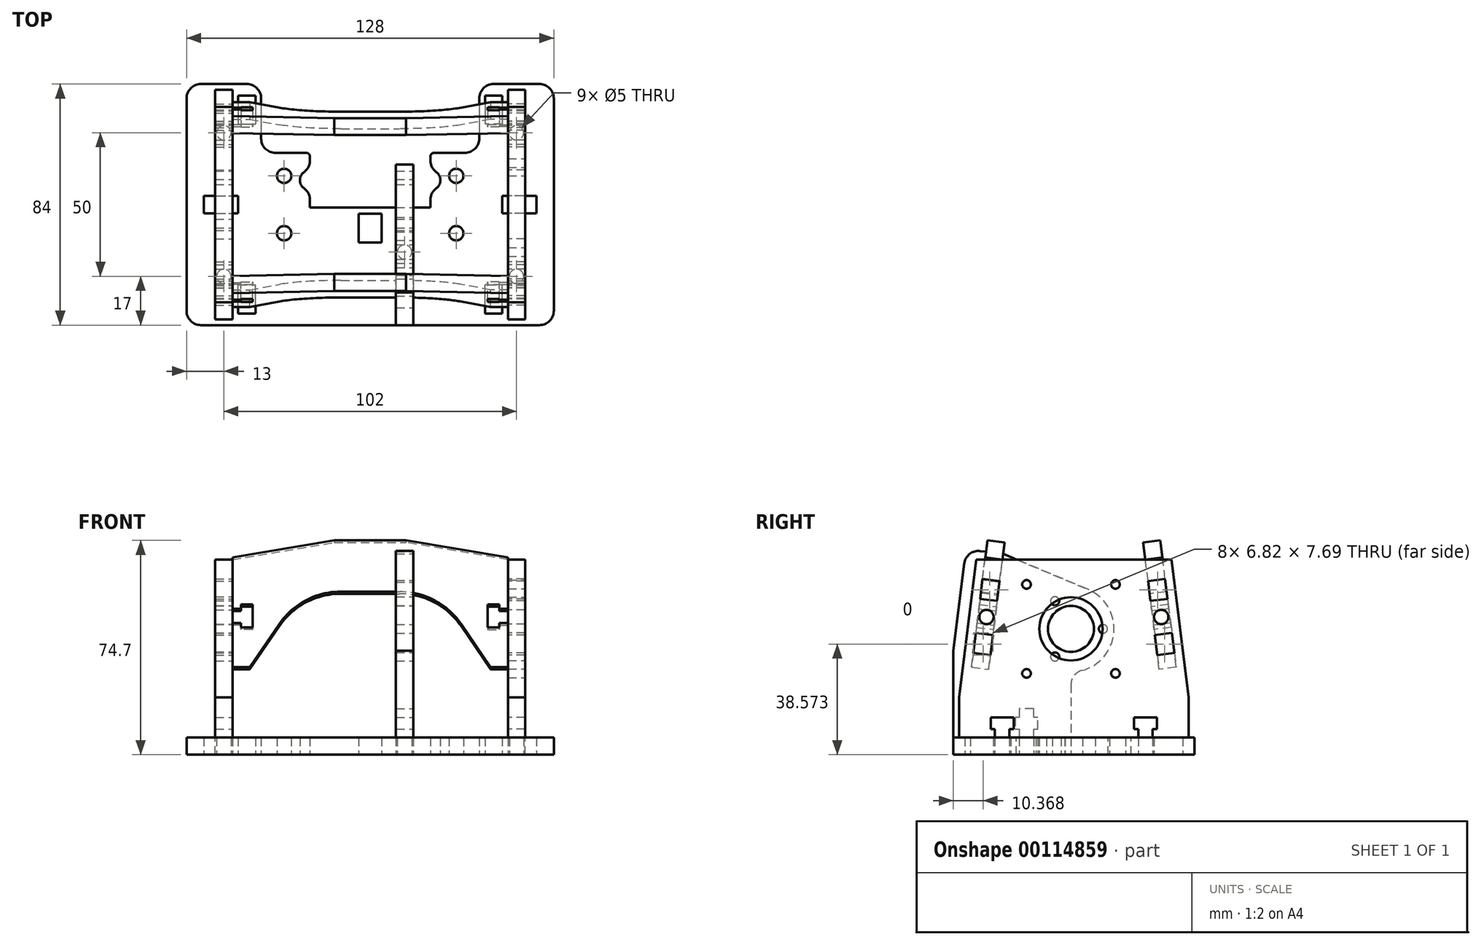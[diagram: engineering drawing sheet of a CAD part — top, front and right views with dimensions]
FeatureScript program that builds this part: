
annotation { "Feature Type Name" : "Feature", "Feature Type Description" : "" }
export const myFeature = defineFeature(function(context is Context, id is Id, definition is map)
    precondition{}
    {
        {
            var Q0;
            Q0=qCreatedBy(makeId("Top.planeOp"),FACE);
            var sketch = newSketch(context, id + "F0", { "sketchPlane" : qUnion([Q0])});
            skLineSegment(sketch, "E0.bottom", {"start": v(-59, 42) * mm, "end": v(-43, 42) * mm});
            skLineSegment(sketch, "E0.top", {"start": v(-59, -42) * mm, "end": v(59, -42) * mm});
            skLineSegment(sketch, "E0.left", {"start": v(-64, 37) * mm, "end": v(-64, -37) * mm});
            skLineSegment(sketch, "E0.right", {"start": v(64, 37) * mm, "end": v(64, -37) * mm});
            skPoint(sketch, "E1", {"position": v(0, 42) * mm});
            skPoint(sketch, "E2", {"position": v(-64, 0) * mm});
            skLineSegment(sketch, "E3.bottom", {"start": v(-46, 38) * mm, "end": v(-40, 38) * mm});
            skLineSegment(sketch, "E3.top", {"start": v(-46, 28) * mm, "end": v(-40, 28) * mm});
            skLineSegment(sketch, "E3.left", {"start": v(-46, 38) * mm, "end": v(-46, 28) * mm});
            skLineSegment(sketch, "E3.right", {"start": v(-40, 38) * mm, "end": v(-40, 28) * mm});
            skLineSegment(sketch, "E4.bottom", {"start": v(-58, 3) * mm, "end": v(-46, 3) * mm});
            skLineSegment(sketch, "E4.top", {"start": v(-58, -3) * mm, "end": v(-46, -3) * mm});
            skLineSegment(sketch, "E4.left", {"start": v(-58, 3) * mm, "end": v(-58, -3) * mm});
            skLineSegment(sketch, "E4.right", {"start": v(-46, 3) * mm, "end": v(-46, -3) * mm});
            skPoint(sketch, "E5", {"position": v(-58, 0) * mm});
            skLineSegment(sketch, "E6.MirrorCS", {"start": v(-40, -38) * mm, "end": v(-40, -28) * mm});
            skLineSegment(sketch, "E7.MirrorCS", {"start": v(-46, -38) * mm, "end": v(-40, -38) * mm});
            skLineSegment(sketch, "E8.MirrorCS", {"start": v(-46, -28) * mm, "end": v(-40, -28) * mm});
            skLineSegment(sketch, "E9.MirrorCS", {"start": v(-46, -38) * mm, "end": v(-46, -28) * mm});
            skLineSegment(sketch, "E10.MirrorCS", {"start": v(58, 3) * mm, "end": v(58, -3) * mm});
            skLineSegment(sketch, "E11.MirrorCS", {"start": v(58, 3) * mm, "end": v(46, 3) * mm});
            skLineSegment(sketch, "E12.MirrorCS", {"start": v(40, 38) * mm, "end": v(40, 28) * mm});
            skLineSegment(sketch, "E13.MirrorCS", {"start": v(46, 38) * mm, "end": v(46, 28) * mm});
            skLineSegment(sketch, "E14.MirrorCS", {"start": v(46, -38) * mm, "end": v(40, -38) * mm});
            skLineSegment(sketch, "E15.MirrorCS", {"start": v(46, -38) * mm, "end": v(46, -28) * mm});
            skLineSegment(sketch, "E16.MirrorCS", {"start": v(46, -28) * mm, "end": v(40, -28) * mm});
            skLineSegment(sketch, "E17.MirrorCS", {"start": v(40, -38) * mm, "end": v(40, -28) * mm});
            skPoint(sketch, "E18.MirrorP", {"position": v(58, 0) * mm});
            skLineSegment(sketch, "E19.MirrorCS", {"start": v(46, 38) * mm, "end": v(40, 38) * mm});
            skLineSegment(sketch, "E20.MirrorCS", {"start": v(58, -3) * mm, "end": v(46, -3) * mm});
            skLineSegment(sketch, "E21.MirrorCS", {"start": v(46, 28) * mm, "end": v(40, 28) * mm});
            skLineSegment(sketch, "E22.MirrorCS", {"start": v(46, 3) * mm, "end": v(46, -3) * mm});
            skCircle(sketch, "E23", {"center": v(-30, 10) * mm, "radius": 2.5 * mm});
            skCircle(sketch, "E24", {"center": v(-30, -10) * mm, "radius": 2.5 * mm});
            skCircle(sketch, "E25", {"center": v(-10, -10) * mm, "radius": 2.5 * mm, "construction": true});
            skCircle(sketch, "E26.MirrorC", {"center": v(30, -10) * mm, "radius": 2.5 * mm});
            skCircle(sketch, "E27.MirrorC", {"center": v(30, 10) * mm, "radius": 2.5 * mm});
            skCircle(sketch, "E28.MirrorC", {"center": v(10, -10) * mm, "radius": 2.5 * mm, "construction": true});
            skPoint(sketch, "E29.visualSharp", {"position": v(-64, 42) * mm});
            skArc(sketch, "E29.filletArc", {"start": v(-59, 42) * mm, "mid": v(-62.54, 40.54) * mm, "end": v(-64, 37) * mm});
            skPoint(sketch, "E30.visualSharp", {"position": v(64, 42) * mm});
            skArc(sketch, "E30.filletArc", {"start": v(64, 37) * mm, "mid": v(62.54, 40.54) * mm, "end": v(59, 42) * mm});
            skPoint(sketch, "E31.visualSharp", {"position": v(64, -42) * mm});
            skArc(sketch, "E31.filletArc", {"start": v(59, -42) * mm, "mid": v(62.54, -40.54) * mm, "end": v(64, -37) * mm});
            skPoint(sketch, "E32.visualSharp", {"position": v(-64, -42) * mm});
            skArc(sketch, "E32.filletArc", {"start": v(-64, -37) * mm, "mid": v(-62.54, -40.54) * mm, "end": v(-59, -42) * mm});
            skLineSegment(sketch, "E33", {"start": v(-38, 37) * mm, "end": v(-38, 23) * mm});
            skLineSegment(sketch, "E34", {"start": v(-33, 18) * mm, "end": v(-22.2, 18) * mm});
            skLineSegment(sketch, "E35", {"start": v(-21, 16.8) * mm, "end": v(-21, 15.37) * mm});
            skLineSegment(sketch, "E36", {"start": v(-21, -1) * mm, "end": v(21, -1) * mm});
            skArc(sketch, "E37", {"start": v(-23.06, 11.33) * mm, "mid": v(-24.5, 8.5) * mm, "end": v(-23.06, 5.67) * mm});
            skLineSegment(sketch, "E38.MirrorCS", {"start": v(38, 37) * mm, "end": v(38, 23) * mm});
            skLineSegment(sketch, "E39.MirrorCS", {"start": v(33, 18) * mm, "end": v(22.2, 18) * mm});
            skArc(sketch, "E40.MirrorCS", {"start": v(23.06, 11.33) * mm, "mid": v(24.5, 8.5) * mm, "end": v(23.06, 5.67) * mm});
            skLineSegment(sketch, "E41.trimOffspring", {"start": v(43, 42) * mm, "end": v(59, 42) * mm});
            skLineSegment(sketch, "E42.trimOffspring", {"start": v(-21, 1.63) * mm, "end": v(-21, -1) * mm});
            skLineSegment(sketch, "E43", {"start": v(21, 15.37) * mm, "end": v(21, 16.8) * mm});
            skLineSegment(sketch, "E44", {"start": v(21, 1.63) * mm, "end": v(21, -1) * mm});
            skPoint(sketch, "E45.visualSharp", {"position": v(-38, 18) * mm});
            skArc(sketch, "E45.filletArc", {"start": v(-38, 23) * mm, "mid": v(-36.54, 19.46) * mm, "end": v(-33, 18) * mm});
            skPoint(sketch, "E46.visualSharp", {"position": v(38, 18) * mm});
            skArc(sketch, "E46.filletArc", {"start": v(33, 18) * mm, "mid": v(36.54, 19.46) * mm, "end": v(38, 23) * mm});
            skPoint(sketch, "E47.visualSharp", {"position": v(38, 42) * mm});
            skArc(sketch, "E47.filletArc", {"start": v(43, 42) * mm, "mid": v(39.46, 40.54) * mm, "end": v(38, 37) * mm});
            skPoint(sketch, "E48.visualSharp", {"position": v(-38, 42) * mm});
            skArc(sketch, "E48.filletArc", {"start": v(-38, 37) * mm, "mid": v(-39.46, 40.54) * mm, "end": v(-43, 42) * mm});
            skPoint(sketch, "E49.visualSharp", {"position": v(-21, 5) * mm});
            skArc(sketch, "E49.filletArc", {"start": v(-21, 1.63) * mm, "mid": v(-21.54, 3.9) * mm, "end": v(-23.06, 5.67) * mm});
            skPoint(sketch, "E50.visualSharp", {"position": v(-21, 12) * mm});
            skArc(sketch, "E50.filletArc", {"start": v(-23.06, 11.33) * mm, "mid": v(-21.54, 13.1) * mm, "end": v(-21, 15.37) * mm});
            skPoint(sketch, "E51.visualSharp", {"position": v(21, 12) * mm});
            skArc(sketch, "E51.filletArc", {"start": v(21, 15.37) * mm, "mid": v(21.54, 13.1) * mm, "end": v(23.06, 11.33) * mm});
            skPoint(sketch, "E52.visualSharp", {"position": v(21, 5) * mm});
            skArc(sketch, "E52.filletArc", {"start": v(23.06, 5.67) * mm, "mid": v(21.54, 3.9) * mm, "end": v(21, 1.63) * mm});
            skPoint(sketch, "E53.visualSharp", {"position": v(-21, 18) * mm});
            skArc(sketch, "E53.filletArc", {"start": v(-21, 16.8) * mm, "mid": v(-21.35, 17.65) * mm, "end": v(-22.2, 18) * mm});
            skPoint(sketch, "E54.visualSharp", {"position": v(21, 18) * mm});
            skArc(sketch, "E54.filletArc", {"start": v(22.2, 18) * mm, "mid": v(21.35, 17.65) * mm, "end": v(21, 16.8) * mm});
            skLineSegment(sketch, "E55.bottom", {"start": v(-4, -3.2) * mm, "end": v(4, -3.2) * mm});
            skLineSegment(sketch, "E55.top", {"start": v(-4, -13.2) * mm, "end": v(4, -13.2) * mm});
            skLineSegment(sketch, "E55.left", {"start": v(-4, -3.2) * mm, "end": v(-4, -13.2) * mm});
            skLineSegment(sketch, "E55.right", {"start": v(4, -3.2) * mm, "end": v(4, -13.2) * mm});
            skPoint(sketch, "E56", {"position": v(0, -3.2) * mm});
            skLineSegment(sketch, "E57.bottom", {"start": v(-23, -4.5) * mm, "end": v(-17, -4.5) * mm, "construction": true});
            skLineSegment(sketch, "E57.top", {"start": v(-23, -9.5) * mm, "end": v(-17, -9.5) * mm, "construction": true});
            skLineSegment(sketch, "E57.left", {"start": v(-23, -4.5) * mm, "end": v(-23, -9.5) * mm, "construction": true});
            skLineSegment(sketch, "E57.right", {"start": v(-17, -4.5) * mm, "end": v(-17, -9.5) * mm, "construction": true});
            skLineSegment(sketch, "E58.bottom", {"start": v(9, -4.5) * mm, "end": v(15, -4.5) * mm});
            skLineSegment(sketch, "E58.top", {"start": v(9, -9.5) * mm, "end": v(15, -9.5) * mm});
            skLineSegment(sketch, "E58.left", {"start": v(9, -4.5) * mm, "end": v(9, -9.5) * mm});
            skLineSegment(sketch, "E58.right", {"start": v(15, -4.5) * mm, "end": v(15, -9.5) * mm});
            skLineSegment(sketch, "E59.bottom", {"start": v(-23, -22) * mm, "end": v(-17, -22) * mm, "construction": true});
            skLineSegment(sketch, "E59.top", {"start": v(-23, -36) * mm, "end": v(-17, -36) * mm, "construction": true});
            skLineSegment(sketch, "E59.left", {"start": v(-23, -22) * mm, "end": v(-23, -36) * mm, "construction": true});
            skLineSegment(sketch, "E59.right", {"start": v(-17, -22) * mm, "end": v(-17, -36) * mm, "construction": true});
            skLineSegment(sketch, "E60.bottom", {"start": v(9, -22) * mm, "end": v(15, -22) * mm});
            skLineSegment(sketch, "E60.top", {"start": v(9, -36) * mm, "end": v(15, -36) * mm});
            skLineSegment(sketch, "E60.left", {"start": v(9, -22) * mm, "end": v(9, -36) * mm});
            skLineSegment(sketch, "E60.right", {"start": v(15, -22) * mm, "end": v(15, -36) * mm});
            skLineSegment(sketch, "E61.bottom", {"start": v(-54, 20) * mm, "end": v(-48, 20) * mm});
            skLineSegment(sketch, "E61.top", {"start": v(-54, 12) * mm, "end": v(-48, 12) * mm});
            skLineSegment(sketch, "E61.left", {"start": v(-54, 20) * mm, "end": v(-54, 12) * mm});
            skLineSegment(sketch, "E61.right", {"start": v(-48, 20) * mm, "end": v(-48, 12) * mm});
            skCircle(sketch, "E62", {"center": v(-51, 25) * mm, "radius": 2.5 * mm});
            skPoint(sketch, "E63", {"position": v(-51, 20) * mm});
            skLineSegment(sketch, "E64.MirrorCS", {"start": v(54, 20) * mm, "end": v(48, 20) * mm});
            skPoint(sketch, "E65.MirrorP", {"position": v(51, 20) * mm});
            skLineSegment(sketch, "E66.MirrorCS", {"start": v(54, 12) * mm, "end": v(48, 12) * mm});
            skLineSegment(sketch, "E67.MirrorCS", {"start": v(48, 20) * mm, "end": v(48, 12) * mm});
            skLineSegment(sketch, "E68.MirrorCS", {"start": v(54, 20) * mm, "end": v(54, 12) * mm});
            skCircle(sketch, "E69.MirrorC", {"center": v(51, 25) * mm, "radius": 2.5 * mm});
            skLineSegment(sketch, "E70.MirrorCS", {"start": v(-54, -20) * mm, "end": v(-48, -20) * mm});
            skLineSegment(sketch, "E71.MirrorCS", {"start": v(-48, -20) * mm, "end": v(-48, -12) * mm});
            skPoint(sketch, "E72.MirrorP", {"position": v(-51, -20) * mm});
            skLineSegment(sketch, "E73.MirrorCS", {"start": v(-54, -12) * mm, "end": v(-48, -12) * mm});
            skCircle(sketch, "E74.MirrorC", {"center": v(-51, -25) * mm, "radius": 2.5 * mm});
            skLineSegment(sketch, "E75.MirrorCS", {"start": v(-54, -20) * mm, "end": v(-54, -12) * mm});
            skPoint(sketch, "E76.MirrorP", {"position": v(51, -20) * mm});
            skLineSegment(sketch, "E77.MirrorCS", {"start": v(54, -20) * mm, "end": v(48, -20) * mm});
            skLineSegment(sketch, "E78.MirrorCS", {"start": v(54, -12) * mm, "end": v(48, -12) * mm});
            skCircle(sketch, "E79.MirrorC", {"center": v(51, -25) * mm, "radius": 2.5 * mm});
            skLineSegment(sketch, "E80.MirrorCS", {"start": v(54, -20) * mm, "end": v(54, -12) * mm});
            skLineSegment(sketch, "E81.MirrorCS", {"start": v(48, -20) * mm, "end": v(48, -12) * mm});
            skPoint(sketch, "E82", {"position": v(12, -9.5) * mm});
            skCircle(sketch, "E83", {"center": v(12, -16.5) * mm, "radius": 2.5 * mm});
            skSolve(sketch);
        }
        {
            var Q0;
            Q0 = qSketchRegion(id + "F0", true);
            extrude(context, id + "F1", {"entities" : qUnion([Q0]), "depth" : 6 * mm});
        }
        {
            var Q0;
            Q0=makeQuery(id+"F1.opExtrude","SWEPT_FACE",FACE,{"disambiguationData":[OSD([sQuery(id+"F0.wireOp",EDGE,"E61.right")])]});
            var sketch = newSketch(context, id + "F2", { "sketchPlane" : qUnion([Q0])});
            skLineSegment(sketch, "E84", {"start": v(-22.5, 6) * mm, "end": v(-20, 6) * mm});
            skLineSegment(sketch, "E85", {"start": v(-20, 6) * mm, "end": v(-20, 0) * mm});
            skLineSegment(sketch, "E86", {"start": v(-20, 0) * mm, "end": v(-12, 0) * mm});
            skLineSegment(sketch, "E87", {"start": v(-12, 0) * mm, "end": v(-12, 6) * mm});
            skLineSegment(sketch, "E88", {"start": v(-12, 6) * mm, "end": v(12, 6) * mm});
            skLineSegment(sketch, "E89", {"start": v(-22.5, 6) * mm, "end": v(-22.5, 9) * mm});
            skLineSegment(sketch, "E90", {"start": v(-22.5, 9) * mm, "end": v(-21, 9) * mm});
            skLineSegment(sketch, "E91", {"start": v(-21, 9) * mm, "end": v(-21, 13) * mm});
            skLineSegment(sketch, "E92", {"start": v(-29, 13) * mm, "end": v(-29, 9) * mm});
            skLineSegment(sketch, "E93", {"start": v(-29, 9) * mm, "end": v(-27.5, 9) * mm});
            skLineSegment(sketch, "E94", {"start": v(-27.5, 9) * mm, "end": v(-27.5, 6) * mm});
            skLineSegment(sketch, "E95", {"start": v(-27.5, 6) * mm, "end": v(-40, 6) * mm});
            skLineSegment(sketch, "E96", {"start": v(-40, 6) * mm, "end": v(-40, 20) * mm});
            skLineSegment(sketch, "E97", {"start": v(-40, 20) * mm, "end": v(-34, 68) * mm});
            skLineSegment(sketch, "E98", {"start": v(-34, 68) * mm, "end": v(34, 68) * mm});
            skPoint(sketch, "E99", {"position": v(0, 68) * mm});
            skLineSegment(sketch, "E100.MirrorCS", {"start": v(21, 9) * mm, "end": v(21, 13) * mm});
            skLineSegment(sketch, "E101.MirrorCS", {"start": v(22.5, 9) * mm, "end": v(21, 9) * mm});
            skLineSegment(sketch, "E102.MirrorCS", {"start": v(22.5, 6) * mm, "end": v(22.5, 9) * mm});
            skLineSegment(sketch, "E103.MirrorCS", {"start": v(29, 9) * mm, "end": v(27.5, 9) * mm});
            skLineSegment(sketch, "E104.MirrorCS", {"start": v(22.5, 6) * mm, "end": v(20, 6) * mm});
            skLineSegment(sketch, "E105.MirrorCS", {"start": v(27.5, 9) * mm, "end": v(27.5, 6) * mm});
            skLineSegment(sketch, "E106.MirrorCS", {"start": v(29, 13) * mm, "end": v(29, 9) * mm});
            skLineSegment(sketch, "E107.MirrorCS", {"start": v(20, 6) * mm, "end": v(20, 0) * mm});
            skLineSegment(sketch, "E108.MirrorCS", {"start": v(40, 6) * mm, "end": v(40, 20) * mm});
            skLineSegment(sketch, "E109.MirrorCS", {"start": v(40, 20) * mm, "end": v(34, 68) * mm});
            skLineSegment(sketch, "E110.MirrorCS", {"start": v(27.5, 6) * mm, "end": v(40, 6) * mm});
            skLineSegment(sketch, "E111.MirrorCS", {"start": v(20, 0) * mm, "end": v(12, 0) * mm});
            skLineSegment(sketch, "E112.MirrorCS", {"start": v(12, 0) * mm, "end": v(12, 6) * mm});
            skCircle(sketch, "E113", {"center": v(-30.45, 48) * mm, "radius": 2.5 * mm});
            skLineSegment(sketch, "E114", {"start": v(-32.69, 54.33) * mm, "end": v(-26.73, 53.58) * mm});
            skLineSegment(sketch, "E115", {"start": v(-26.73, 53.58) * mm, "end": v(-25.86, 60.53) * mm});
            skLineSegment(sketch, "E116", {"start": v(-25.86, 60.53) * mm, "end": v(-31.82, 61.27) * mm});
            skLineSegment(sketch, "E117", {"start": v(-31.82, 61.27) * mm, "end": v(-32.69, 54.33) * mm});
            skPoint(sketch, "E118", {"position": v(-29.7, 53.95) * mm});
            skLineSegment(sketch, "E119", {"start": v(-30.45, 48) * mm, "end": v(-29.7, 53.95) * mm, "construction": true});
            skLineSegment(sketch, "E120", {"start": v(-30.45, 48) * mm, "end": v(-27.97, 47.69) * mm, "construction": true});
            skLineSegment(sketch, "E121.MirrorCS", {"start": v(-34.17, 42.42) * mm, "end": v(-28.22, 41.67) * mm});
            skLineSegment(sketch, "E122.MirrorCS", {"start": v(-28.22, 41.67) * mm, "end": v(-29.09, 34.73) * mm});
            skLineSegment(sketch, "E123.MirrorCS", {"start": v(-35.04, 35.47) * mm, "end": v(-34.17, 42.42) * mm});
            skLineSegment(sketch, "E124.MirrorCS", {"start": v(-29.09, 34.73) * mm, "end": v(-35.04, 35.47) * mm});
            skPoint(sketch, "E125.MirrorP", {"position": v(-31.2, 42.05) * mm});
            skLineSegment(sketch, "E126.MirrorCS", {"start": v(32.69, 54.33) * mm, "end": v(26.73, 53.58) * mm});
            skLineSegment(sketch, "E127.MirrorCS", {"start": v(30.45, 48) * mm, "end": v(27.97, 47.69) * mm, "construction": true});
            skLineSegment(sketch, "E128.MirrorCS", {"start": v(34.17, 42.42) * mm, "end": v(28.22, 41.67) * mm});
            skLineSegment(sketch, "E129.MirrorCS", {"start": v(31.82, 61.27) * mm, "end": v(32.69, 54.33) * mm});
            skPoint(sketch, "E130.MirrorP", {"position": v(31.2, 42.05) * mm});
            skLineSegment(sketch, "E131.MirrorCS", {"start": v(30.45, 48) * mm, "end": v(29.7, 53.95) * mm, "construction": true});
            skLineSegment(sketch, "E132.MirrorCS", {"start": v(29.09, 34.73) * mm, "end": v(35.04, 35.47) * mm});
            skLineSegment(sketch, "E133.MirrorCS", {"start": v(35.04, 35.47) * mm, "end": v(34.17, 42.42) * mm});
            skCircle(sketch, "E134.MirrorC", {"center": v(30.45, 48) * mm, "radius": 2.5 * mm});
            skLineSegment(sketch, "E135.MirrorCS", {"start": v(25.86, 60.53) * mm, "end": v(31.82, 61.27) * mm});
            skPoint(sketch, "E136.MirrorP", {"position": v(29.7, 53.95) * mm});
            skLineSegment(sketch, "E137.MirrorCS", {"start": v(26.73, 53.58) * mm, "end": v(25.86, 60.53) * mm});
            skLineSegment(sketch, "E138.MirrorCS", {"start": v(28.22, 41.67) * mm, "end": v(29.09, 34.73) * mm});
            skLineSegment(sketch, "E139", {"start": v(-29, 13) * mm, "end": v(-21, 13) * mm});
            skLineSegment(sketch, "E140", {"start": v(21, 13) * mm, "end": v(29, 13) * mm});
            skSolve(sketch);
        }
        {
            var Q0;
            Q0 = qSketchRegion(id + "F2", true);
            var Q1;
            Q1=makeQuery(id+"F1.opExtrude","SWEPT_FACE",FACE,{"disambiguationData":[OSD([sQuery(id+"F0.wireOp",EDGE,"E61.left")])]});
            extrude(context, id + "F3", {"entities" : qUnion([Q0]), "endBound" : BoundingType.UP_TO_SURFACE, "endBoundEntityFace" : qUnion([Q1]), "depth" : 25 * mm});
        }
        {
            var Q0;
            Q0=makeQuery(id+"F3.opExtrude","SWEPT_BODY",BODY,{"disambiguationData":[OSD([sQuery(id+"F2.wireOp",EDGE,"E84"),sQuery(id+"F2.wireOp",EDGE,"E85"),sQuery(id+"F2.wireOp",EDGE,"E86"),sQuery(id+"F2.wireOp",EDGE,"E87"),sQuery(id+"F2.wireOp",EDGE,"E88"),sQuery(id+"F2.wireOp",EDGE,"E89"),sQuery(id+"F2.wireOp",EDGE,"E90"),sQuery(id+"F2.wireOp",EDGE,"E91"),sQuery(id+"F2.wireOp",EDGE,"E92"),sQuery(id+"F2.wireOp",EDGE,"E93"),sQuery(id+"F2.wireOp",EDGE,"E94"),sQuery(id+"F2.wireOp",EDGE,"E95"),sQuery(id+"F2.wireOp",EDGE,"E96"),sQuery(id+"F2.wireOp",EDGE,"E97"),sQuery(id+"F2.wireOp",EDGE,"E98"),sQuery(id+"F2.wireOp",EDGE,"E100.MirrorCS"),sQuery(id+"F2.wireOp",EDGE,"E101.MirrorCS"),sQuery(id+"F2.wireOp",EDGE,"E102.MirrorCS"),sQuery(id+"F2.wireOp",EDGE,"E103.MirrorCS"),sQuery(id+"F2.wireOp",EDGE,"E104.MirrorCS"),sQuery(id+"F2.wireOp",EDGE,"E105.MirrorCS"),sQuery(id+"F2.wireOp",EDGE,"E106.MirrorCS"),sQuery(id+"F2.wireOp",EDGE,"E107.MirrorCS"),sQuery(id+"F2.wireOp",EDGE,"E108.MirrorCS"),sQuery(id+"F2.wireOp",EDGE,"E109.MirrorCS"),sQuery(id+"F2.wireOp",EDGE,"E110.MirrorCS"),sQuery(id+"F2.wireOp",EDGE,"E111.MirrorCS"),sQuery(id+"F2.wireOp",EDGE,"E112.MirrorCS"),sQuery(id+"F2.wireOp",EDGE,"E113"),sQuery(id+"F2.wireOp",EDGE,"E114"),sQuery(id+"F2.wireOp",EDGE,"E115"),sQuery(id+"F2.wireOp",EDGE,"E116"),sQuery(id+"F2.wireOp",EDGE,"E117"),sQuery(id+"F2.wireOp",EDGE,"E121.MirrorCS"),sQuery(id+"F2.wireOp",EDGE,"E122.MirrorCS"),sQuery(id+"F2.wireOp",EDGE,"E123.MirrorCS"),sQuery(id+"F2.wireOp",EDGE,"E124.MirrorCS"),sQuery(id+"F2.wireOp",EDGE,"E126.MirrorCS"),sQuery(id+"F2.wireOp",EDGE,"E128.MirrorCS"),sQuery(id+"F2.wireOp",EDGE,"E129.MirrorCS"),sQuery(id+"F2.wireOp",EDGE,"E132.MirrorCS"),sQuery(id+"F2.wireOp",EDGE,"E133.MirrorCS"),sQuery(id+"F2.wireOp",EDGE,"E134.MirrorC"),sQuery(id+"F2.wireOp",EDGE,"E135.MirrorCS"),sQuery(id+"F2.wireOp",EDGE,"E137.MirrorCS"),sQuery(id+"F2.wireOp",EDGE,"E138.MirrorCS"),sQuery(id+"F2.wireOp",EDGE,"E139"),sQuery(id+"F2.wireOp",EDGE,"E140")])]});
            var Q1;
            Q1=qCreatedBy(makeId("Right.planeOp"),FACE);
            mirror(context, id + "F4", {"entities" : qUnion([Q0]), "mirrorPlane" : qUnion([Q1])});
        }
        {
            var Q0;
            Q0=makeQuery(id+"F3.opExtrude","SWEPT_FACE",FACE,{"disambiguationData":[OSD([sQuery(id+"F2.wireOp",EDGE,"E137.MirrorCS")])]});
            var sketch = newSketch(context, id + "F5", { "sketchPlane" : qUnion([Q0])});
            skLineSegment(sketch, "E141", {"start": v(-54, 56.85) * mm, "end": v(-48, 56.85) * mm});
            skLineSegment(sketch, "E142", {"start": v(-48, 56.85) * mm, "end": v(-48, 64.38) * mm});
            skLineSegment(sketch, "E143", {"start": v(-48, 64.38) * mm, "end": v(-12.5, 70.38) * mm});
            skLineSegment(sketch, "E144", {"start": v(-12.5, 70.38) * mm, "end": v(12.5, 70.38) * mm});
            skPoint(sketch, "E145", {"position": v(0, 70.38) * mm});
            skLineSegment(sketch, "E146", {"start": v(-54, 56.85) * mm, "end": v(-54, 49.85) * mm});
            skLineSegment(sketch, "E147", {"start": v(-54, 49.85) * mm, "end": v(-48, 49.85) * mm});
            skLineSegment(sketch, "E148", {"start": v(-48, 49.85) * mm, "end": v(-48, 46.35) * mm});
            skLineSegment(sketch, "E149", {"start": v(-48, 46.35) * mm, "end": v(-45, 46.35) * mm});
            skLineSegment(sketch, "E150", {"start": v(-45, 46.35) * mm, "end": v(-45, 47.85) * mm});
            skLineSegment(sketch, "E151", {"start": v(-45, 47.85) * mm, "end": v(-41, 47.85) * mm});
            skLineSegment(sketch, "E152", {"start": v(-41, 39.85) * mm, "end": v(-45, 39.85) * mm});
            skLineSegment(sketch, "E153", {"start": v(-45, 39.85) * mm, "end": v(-45, 41.35) * mm});
            skLineSegment(sketch, "E154", {"start": v(-45, 41.35) * mm, "end": v(-48, 41.35) * mm});
            skLineSegment(sketch, "E155", {"start": v(-48, 41.35) * mm, "end": v(-48, 37.85) * mm});
            skLineSegment(sketch, "E156", {"start": v(-48, 37.85) * mm, "end": v(-54, 37.85) * mm});
            skLineSegment(sketch, "E157", {"start": v(-54, 37.85) * mm, "end": v(-54, 30.85) * mm});
            skLineSegment(sketch, "E158", {"start": v(-54, 30.85) * mm, "end": v(-48, 30.85) * mm});
            skLineSegment(sketch, "E159", {"start": v(-48, 30.85) * mm, "end": v(-48, 25.85) * mm});
            skLineSegment(sketch, "E160", {"start": v(-48, 25.85) * mm, "end": v(-42, 25.85) * mm});
            skLineSegment(sketch, "E161", {"start": v(-42, 25.85) * mm, "end": v(-31.74, 40.98) * mm});
            skLineSegment(sketch, "E162", {"start": v(-10.22, 52.38) * mm, "end": v(10.22, 52.38) * mm});
            skPoint(sketch, "E163", {"position": v(0, 52.38) * mm});
            skLineSegment(sketch, "E164.MirrorCS", {"start": v(45, 39.85) * mm, "end": v(45, 41.35) * mm});
            skLineSegment(sketch, "E165.MirrorCS", {"start": v(45, 46.35) * mm, "end": v(45, 47.85) * mm});
            skLineSegment(sketch, "E166.MirrorCS", {"start": v(48, 30.85) * mm, "end": v(48, 25.85) * mm});
            skLineSegment(sketch, "E167.MirrorCS", {"start": v(54, 49.85) * mm, "end": v(48, 49.85) * mm});
            skLineSegment(sketch, "E168.MirrorCS", {"start": v(48, 49.85) * mm, "end": v(48, 46.35) * mm});
            skLineSegment(sketch, "E169.MirrorCS", {"start": v(48, 46.35) * mm, "end": v(45, 46.35) * mm});
            skLineSegment(sketch, "E170.MirrorCS", {"start": v(54, 56.85) * mm, "end": v(48, 56.85) * mm});
            skLineSegment(sketch, "E171.MirrorCS", {"start": v(45, 47.85) * mm, "end": v(41, 47.85) * mm});
            skLineSegment(sketch, "E172.MirrorCS", {"start": v(41, 39.85) * mm, "end": v(45, 39.85) * mm});
            skLineSegment(sketch, "E173.MirrorCS", {"start": v(48, 41.35) * mm, "end": v(48, 37.85) * mm});
            skLineSegment(sketch, "E174.MirrorCS", {"start": v(48, 37.85) * mm, "end": v(54, 37.85) * mm});
            skLineSegment(sketch, "E175.MirrorCS", {"start": v(45, 41.35) * mm, "end": v(48, 41.35) * mm});
            skLineSegment(sketch, "E176.MirrorCS", {"start": v(54, 30.85) * mm, "end": v(48, 30.85) * mm});
            skLineSegment(sketch, "E177.MirrorCS", {"start": v(54, 56.85) * mm, "end": v(54, 49.85) * mm});
            skLineSegment(sketch, "E178.MirrorCS", {"start": v(48, 64.38) * mm, "end": v(12.5, 70.38) * mm});
            skLineSegment(sketch, "E179.MirrorCS", {"start": v(48, 25.85) * mm, "end": v(42, 25.85) * mm});
            skLineSegment(sketch, "E180.MirrorCS", {"start": v(48, 56.85) * mm, "end": v(48, 64.38) * mm});
            skLineSegment(sketch, "E181.MirrorCS", {"start": v(54, 37.85) * mm, "end": v(54, 30.85) * mm});
            skLineSegment(sketch, "E182.MirrorCS", {"start": v(42, 25.85) * mm, "end": v(31.74, 40.98) * mm});
            skPoint(sketch, "E183.visualSharp", {"position": v(-24, 52.38) * mm});
            skArc(sketch, "E183.filletArc", {"start": v(-10.22, 52.38) * mm, "mid": v(-22.4, 49.36) * mm, "end": v(-31.74, 40.98) * mm});
            skArc(sketch, "E184.filletArc", {"start": v(31.74, 40.98) * mm, "mid": v(22.4, 49.36) * mm, "end": v(10.22, 52.38) * mm});
            skLineSegment(sketch, "E185", {"start": v(-41, 47.85) * mm, "end": v(-41, 39.85) * mm});
            skLineSegment(sketch, "E186", {"start": v(41, 47.85) * mm, "end": v(41, 39.85) * mm});
            skSolve(sketch);
        }
        {
            var Q0;
            Q0 = qSketchRegion(id + "F5", true);
            var Q1;
            Q1=makeQuery(id+"F3.opExtrude","SWEPT_FACE",FACE,{"disambiguationData":[OSD([sQuery(id+"F2.wireOp",EDGE,"E129.MirrorCS")])]});
            extrude(context, id + "F6", {"entities" : qUnion([Q0]), "endBound" : BoundingType.UP_TO_SURFACE, "endBoundEntityFace" : qUnion([Q1]), "depth" : 25 * mm});
        }
        {
            var Q0;
            Q0=makeQuery(id+"F6.opExtrude","SWEPT_BODY",BODY,{"disambiguationData":[OSD([sQuery(id+"F5.wireOp",EDGE,"E141"),sQuery(id+"F5.wireOp",EDGE,"E142"),sQuery(id+"F5.wireOp",EDGE,"E143"),sQuery(id+"F5.wireOp",EDGE,"E144"),sQuery(id+"F5.wireOp",EDGE,"E146"),sQuery(id+"F5.wireOp",EDGE,"E147"),sQuery(id+"F5.wireOp",EDGE,"E148"),sQuery(id+"F5.wireOp",EDGE,"E149"),sQuery(id+"F5.wireOp",EDGE,"E150"),sQuery(id+"F5.wireOp",EDGE,"E151"),sQuery(id+"F5.wireOp",EDGE,"E152"),sQuery(id+"F5.wireOp",EDGE,"E153"),sQuery(id+"F5.wireOp",EDGE,"E154"),sQuery(id+"F5.wireOp",EDGE,"E155"),sQuery(id+"F5.wireOp",EDGE,"E156"),sQuery(id+"F5.wireOp",EDGE,"E157"),sQuery(id+"F5.wireOp",EDGE,"E158"),sQuery(id+"F5.wireOp",EDGE,"E159"),sQuery(id+"F5.wireOp",EDGE,"E160"),sQuery(id+"F5.wireOp",EDGE,"E161"),sQuery(id+"F5.wireOp",EDGE,"E162"),sQuery(id+"F5.wireOp",EDGE,"E164.MirrorCS"),sQuery(id+"F5.wireOp",EDGE,"E165.MirrorCS"),sQuery(id+"F5.wireOp",EDGE,"E166.MirrorCS"),sQuery(id+"F5.wireOp",EDGE,"E167.MirrorCS"),sQuery(id+"F5.wireOp",EDGE,"E168.MirrorCS"),sQuery(id+"F5.wireOp",EDGE,"E169.MirrorCS"),sQuery(id+"F5.wireOp",EDGE,"E170.MirrorCS"),sQuery(id+"F5.wireOp",EDGE,"E171.MirrorCS"),sQuery(id+"F5.wireOp",EDGE,"E172.MirrorCS"),sQuery(id+"F5.wireOp",EDGE,"E173.MirrorCS"),sQuery(id+"F5.wireOp",EDGE,"E174.MirrorCS"),sQuery(id+"F5.wireOp",EDGE,"E175.MirrorCS"),sQuery(id+"F5.wireOp",EDGE,"E176.MirrorCS"),sQuery(id+"F5.wireOp",EDGE,"E177.MirrorCS"),sQuery(id+"F5.wireOp",EDGE,"E178.MirrorCS"),sQuery(id+"F5.wireOp",EDGE,"E179.MirrorCS"),sQuery(id+"F5.wireOp",EDGE,"E180.MirrorCS"),sQuery(id+"F5.wireOp",EDGE,"E181.MirrorCS"),sQuery(id+"F5.wireOp",EDGE,"E182.MirrorCS"),sQuery(id+"F5.wireOp",EDGE,"E183.filletArc"),sQuery(id+"F5.wireOp",EDGE,"E184.filletArc"),sQuery(id+"F5.wireOp",EDGE,"E185"),sQuery(id+"F5.wireOp",EDGE,"E186")])]});
            var Q1;
            Q1=qCreatedBy(makeId("Front.planeOp"),FACE);
            mirror(context, id + "F7", {"entities" : qUnion([Q0]), "mirrorPlane" : qUnion([Q1])});
        }
        {
            var Q0;
            Q0=qCreatedBy(makeId("Front.planeOp"),FACE);
            cPlane(context, id + "F8", {"entities" : qUnion([Q0]), "cplaneType" : CPlaneType.OFFSET, "offset" : 1 * mm, "width" : 150 * mm, "height" : 150 * mm});
        }
        {
            var Q0;
            Q0=makeQuery(id+"F4.opPattern","COPY",FACE,{"derivedFrom":makeQuery(id+"F3.opExtrude","CAP_FACE",FACE,{"disambiguationData":[OSD([sQuery(id+"F2.wireOp",EDGE,"E84"),sQuery(id+"F2.wireOp",EDGE,"E85"),sQuery(id+"F2.wireOp",EDGE,"E86"),sQuery(id+"F2.wireOp",EDGE,"E87"),sQuery(id+"F2.wireOp",EDGE,"E88"),sQuery(id+"F2.wireOp",EDGE,"E89"),sQuery(id+"F2.wireOp",EDGE,"E90"),sQuery(id+"F2.wireOp",EDGE,"E91"),sQuery(id+"F2.wireOp",EDGE,"E92"),sQuery(id+"F2.wireOp",EDGE,"E93"),sQuery(id+"F2.wireOp",EDGE,"E94"),sQuery(id+"F2.wireOp",EDGE,"E95"),sQuery(id+"F2.wireOp",EDGE,"E96"),sQuery(id+"F2.wireOp",EDGE,"E97"),sQuery(id+"F2.wireOp",EDGE,"E98"),sQuery(id+"F2.wireOp",EDGE,"E100.MirrorCS"),sQuery(id+"F2.wireOp",EDGE,"E101.MirrorCS"),sQuery(id+"F2.wireOp",EDGE,"E102.MirrorCS"),sQuery(id+"F2.wireOp",EDGE,"E103.MirrorCS"),sQuery(id+"F2.wireOp",EDGE,"E104.MirrorCS"),sQuery(id+"F2.wireOp",EDGE,"E105.MirrorCS"),sQuery(id+"F2.wireOp",EDGE,"E106.MirrorCS"),sQuery(id+"F2.wireOp",EDGE,"E107.MirrorCS"),sQuery(id+"F2.wireOp",EDGE,"E108.MirrorCS"),sQuery(id+"F2.wireOp",EDGE,"E109.MirrorCS"),sQuery(id+"F2.wireOp",EDGE,"E110.MirrorCS"),sQuery(id+"F2.wireOp",EDGE,"E111.MirrorCS"),sQuery(id+"F2.wireOp",EDGE,"E112.MirrorCS"),sQuery(id+"F2.wireOp",EDGE,"E113"),sQuery(id+"F2.wireOp",EDGE,"E114"),sQuery(id+"F2.wireOp",EDGE,"E115"),sQuery(id+"F2.wireOp",EDGE,"E116"),sQuery(id+"F2.wireOp",EDGE,"E117"),sQuery(id+"F2.wireOp",EDGE,"E121.MirrorCS"),sQuery(id+"F2.wireOp",EDGE,"E122.MirrorCS"),sQuery(id+"F2.wireOp",EDGE,"E123.MirrorCS"),sQuery(id+"F2.wireOp",EDGE,"E124.MirrorCS"),sQuery(id+"F2.wireOp",EDGE,"E126.MirrorCS"),sQuery(id+"F2.wireOp",EDGE,"E128.MirrorCS"),sQuery(id+"F2.wireOp",EDGE,"E129.MirrorCS"),sQuery(id+"F2.wireOp",EDGE,"E132.MirrorCS"),sQuery(id+"F2.wireOp",EDGE,"E133.MirrorCS"),sQuery(id+"F2.wireOp",EDGE,"E134.MirrorC"),sQuery(id+"F2.wireOp",EDGE,"E135.MirrorCS"),sQuery(id+"F2.wireOp",EDGE,"E137.MirrorCS"),sQuery(id+"F2.wireOp",EDGE,"E138.MirrorCS"),sQuery(id+"F2.wireOp",EDGE,"E139"),sQuery(id+"F2.wireOp",EDGE,"E140")])],"isStart":false}),"instanceName":"1"});
            var sketch = newSketch(context, id + "F9", { "sketchPlane" : qUnion([Q0])});
            skCircle(sketch, "E187.cCircle", {"center": v(-1, 43.85) * mm, "radius": 15.5 * mm, "construction": true});
            skLineSegment(sketch, "E187.0", {"start": v(-16.5, 28.35) * mm, "end": v(-16.5, 59.35) * mm, "construction": true});
            skLineSegment(sketch, "E187.1", {"start": v(-16.5, 59.35) * mm, "end": v(14.5, 59.35) * mm, "construction": true});
            skLineSegment(sketch, "E187.2", {"start": v(14.5, 59.35) * mm, "end": v(14.5, 28.35) * mm, "construction": true});
            skLineSegment(sketch, "E187.3", {"start": v(14.5, 28.35) * mm, "end": v(-16.5, 28.35) * mm, "construction": true});
            skPoint(sketch, "E187.0.midPoint", {"position": v(-16.5, 43.85) * mm});
            skCircle(sketch, "E188.cCircle", {"center": v(-1, 43.85) * mm, "radius": 21.15 * mm, "construction": true});
            skLineSegment(sketch, "E188.0", {"start": v(20.15, 65) * mm, "end": v(20.15, 22.7) * mm, "construction": true});
            skLineSegment(sketch, "E188.1", {"start": v(20.15, 22.7) * mm, "end": v(-22.15, 22.7) * mm, "construction": true});
            skLineSegment(sketch, "E188.2", {"start": v(-22.15, 22.7) * mm, "end": v(-22.15, 65) * mm, "construction": true});
            skLineSegment(sketch, "E188.3", {"start": v(-22.15, 65) * mm, "end": v(20.15, 65) * mm, "construction": true});
            skPoint(sketch, "E188.0.midPoint", {"position": v(20.15, 43.85) * mm});
            skCircle(sketch, "E189", {"center": v(-1, 43.85) * mm, "radius": 11 * mm});
            skCircle(sketch, "E190", {"center": v(-16.5, 59.35) * mm, "radius": 1.5 * mm});
            skCircle(sketch, "E191", {"center": v(-16.5, 28.35) * mm, "radius": 1.5 * mm});
            skCircle(sketch, "E192", {"center": v(14.5, 28.35) * mm, "radius": 1.5 * mm});
            skCircle(sketch, "E193", {"center": v(14.5, 59.35) * mm, "radius": 1.5 * mm});
            skSolve(sketch);
        }
        {
            var Q0;
            Q0 = qSketchRegion(id + "F9", true);
            var Q1;
            Q1=makeQuery(id+"F4.opPattern","COPY",FACE,{"derivedFrom":makeQuery(id+"F3.opExtrude","CAP_FACE",FACE,{"disambiguationData":[OSD([sQuery(id+"F2.wireOp",EDGE,"E84"),sQuery(id+"F2.wireOp",EDGE,"E85"),sQuery(id+"F2.wireOp",EDGE,"E86"),sQuery(id+"F2.wireOp",EDGE,"E87"),sQuery(id+"F2.wireOp",EDGE,"E88"),sQuery(id+"F2.wireOp",EDGE,"E89"),sQuery(id+"F2.wireOp",EDGE,"E90"),sQuery(id+"F2.wireOp",EDGE,"E91"),sQuery(id+"F2.wireOp",EDGE,"E92"),sQuery(id+"F2.wireOp",EDGE,"E93"),sQuery(id+"F2.wireOp",EDGE,"E94"),sQuery(id+"F2.wireOp",EDGE,"E95"),sQuery(id+"F2.wireOp",EDGE,"E96"),sQuery(id+"F2.wireOp",EDGE,"E97"),sQuery(id+"F2.wireOp",EDGE,"E98"),sQuery(id+"F2.wireOp",EDGE,"E100.MirrorCS"),sQuery(id+"F2.wireOp",EDGE,"E101.MirrorCS"),sQuery(id+"F2.wireOp",EDGE,"E102.MirrorCS"),sQuery(id+"F2.wireOp",EDGE,"E103.MirrorCS"),sQuery(id+"F2.wireOp",EDGE,"E104.MirrorCS"),sQuery(id+"F2.wireOp",EDGE,"E105.MirrorCS"),sQuery(id+"F2.wireOp",EDGE,"E106.MirrorCS"),sQuery(id+"F2.wireOp",EDGE,"E107.MirrorCS"),sQuery(id+"F2.wireOp",EDGE,"E108.MirrorCS"),sQuery(id+"F2.wireOp",EDGE,"E109.MirrorCS"),sQuery(id+"F2.wireOp",EDGE,"E110.MirrorCS"),sQuery(id+"F2.wireOp",EDGE,"E111.MirrorCS"),sQuery(id+"F2.wireOp",EDGE,"E112.MirrorCS"),sQuery(id+"F2.wireOp",EDGE,"E113"),sQuery(id+"F2.wireOp",EDGE,"E114"),sQuery(id+"F2.wireOp",EDGE,"E115"),sQuery(id+"F2.wireOp",EDGE,"E116"),sQuery(id+"F2.wireOp",EDGE,"E117"),sQuery(id+"F2.wireOp",EDGE,"E121.MirrorCS"),sQuery(id+"F2.wireOp",EDGE,"E122.MirrorCS"),sQuery(id+"F2.wireOp",EDGE,"E123.MirrorCS"),sQuery(id+"F2.wireOp",EDGE,"E124.MirrorCS"),sQuery(id+"F2.wireOp",EDGE,"E126.MirrorCS"),sQuery(id+"F2.wireOp",EDGE,"E128.MirrorCS"),sQuery(id+"F2.wireOp",EDGE,"E129.MirrorCS"),sQuery(id+"F2.wireOp",EDGE,"E132.MirrorCS"),sQuery(id+"F2.wireOp",EDGE,"E133.MirrorCS"),sQuery(id+"F2.wireOp",EDGE,"E134.MirrorC"),sQuery(id+"F2.wireOp",EDGE,"E135.MirrorCS"),sQuery(id+"F2.wireOp",EDGE,"E137.MirrorCS"),sQuery(id+"F2.wireOp",EDGE,"E138.MirrorCS"),sQuery(id+"F2.wireOp",EDGE,"E139"),sQuery(id+"F2.wireOp",EDGE,"E140")])],"isStart":true}),"instanceName":"1"});
            extrude(context, id + "F10", {"entities" : qUnion([Q0]), "operationType" : NewBodyOperationType.REMOVE, "endBound" : BoundingType.UP_TO_SURFACE, "oppositeDirection" : true, "endBoundEntityFace" : qUnion([Q1]), "depth" : 25 * mm});
        }
        {
            var Q0;
            Q0=makeQuery(id+"F1.opExtrude","SWEPT_FACE",FACE,{"disambiguationData":[OSD([sQuery(id+"F0.wireOp",EDGE,"E60.right")])]});
            var sketch = newSketch(context, id + "F11", { "sketchPlane" : qUnion([Q0])});
            skLineSegment(sketch, "E194", {"start": v(36, 0) * mm, "end": v(36, 6) * mm});
            skLineSegment(sketch, "E195", {"start": v(36, 6) * mm, "end": v(42, 6) * mm});
            skLineSegment(sketch, "E196", {"start": v(42, 6) * mm, "end": v(42, 36.25) * mm});
            skLineSegment(sketch, "E197", {"start": v(42, 36.25) * mm, "end": v(38.2, 66.64) * mm});
            skLineSegment(sketch, "E198", {"start": v(32.62, 70.98) * mm, "end": v(30.64, 70.73) * mm});
            skLineSegment(sketch, "E199", {"start": v(30.64, 70.73) * mm, "end": v(31.88, 60.8) * mm});
            skLineSegment(sketch, "E200", {"start": v(31.88, 60.8) * mm, "end": v(25.92, 60.06) * mm});
            skLineSegment(sketch, "E201", {"start": v(25.92, 60.06) * mm, "end": v(24.68, 69.98) * mm});
            skLineSegment(sketch, "E202", {"start": v(24.68, 69.98) * mm, "end": v(-4.78, 57.7) * mm});
            skPoint(sketch, "E203.visualSharp", {"position": v(37.58, 71.6) * mm});
            skArc(sketch, "E203.filletArc", {"start": v(38.2, 66.64) * mm, "mid": v(36.3, 69.96) * mm, "end": v(32.62, 70.98) * mm});
            skCircle(sketch, "E204", {"center": v(1, 43.85) * mm, "radius": 8 * mm});
            skArc(sketch, "E205", {"start": v(-4.78, 57.7) * mm, "mid": v(-13.96, 42.78) * mm, "end": v(-2.75, 29.33) * mm});
            skCircle(sketch, "E206.cCircle", {"center": v(1, 43.85) * mm, "radius": 5.6 * mm, "construction": true});
            skLineSegment(sketch, "E206.0", {"start": v(6.6, 34.15) * mm, "end": v(-10.2, 43.85) * mm, "construction": true});
            skLineSegment(sketch, "E206.1", {"start": v(-10.2, 43.85) * mm, "end": v(6.6, 53.55) * mm, "construction": true});
            skLineSegment(sketch, "E206.2", {"start": v(6.6, 53.55) * mm, "end": v(6.6, 34.15) * mm, "construction": true});
            skPoint(sketch, "E206.0.midPoint", {"position": v(-1.8, 39) * mm});
            skCircle(sketch, "E207", {"center": v(1, 43.85) * mm, "radius": 9 * mm, "construction": true});
            skCircle(sketch, "E208", {"center": v(-10.2, 43.85) * mm, "radius": 1.5 * mm});
            skCircle(sketch, "E209", {"center": v(6.6, 34.15) * mm, "radius": 1.5 * mm});
            skCircle(sketch, "E210", {"center": v(6.6, 53.55) * mm, "radius": 1.5 * mm});
            skLineSegment(sketch, "E211", {"start": v(36, 0) * mm, "end": v(22, 0) * mm});
            skLineSegment(sketch, "E212", {"start": v(22, 0) * mm, "end": v(22, 6) * mm});
            skLineSegment(sketch, "E213", {"start": v(22, 6) * mm, "end": v(19, 6) * mm});
            skLineSegment(sketch, "E214", {"start": v(19, 6) * mm, "end": v(19, 9) * mm});
            skLineSegment(sketch, "E215", {"start": v(19, 9) * mm, "end": v(20.5, 9) * mm});
            skLineSegment(sketch, "E216", {"start": v(20.5, 9) * mm, "end": v(20.5, 13) * mm});
            skLineSegment(sketch, "E217", {"start": v(20.5, 13) * mm, "end": v(19, 13) * mm});
            skLineSegment(sketch, "E218", {"start": v(19, 13) * mm, "end": v(19, 16) * mm});
            skLineSegment(sketch, "E219", {"start": v(19, 16) * mm, "end": v(14, 16) * mm});
            skLineSegment(sketch, "E220", {"start": v(14, 16) * mm, "end": v(14, 13) * mm});
            skLineSegment(sketch, "E221", {"start": v(14, 13) * mm, "end": v(12.5, 13) * mm});
            skLineSegment(sketch, "E222", {"start": v(12.5, 13) * mm, "end": v(12.5, 9) * mm});
            skLineSegment(sketch, "E223", {"start": v(12.5, 9) * mm, "end": v(14, 9) * mm});
            skLineSegment(sketch, "E224", {"start": v(14, 9) * mm, "end": v(14, 6) * mm});
            skLineSegment(sketch, "E225", {"start": v(14, 6) * mm, "end": v(9.5, 6) * mm});
            skLineSegment(sketch, "E226", {"start": v(9.5, 6) * mm, "end": v(9.5, 0) * mm});
            skLineSegment(sketch, "E227", {"start": v(9.5, 0) * mm, "end": v(4.5, 0) * mm});
            skLineSegment(sketch, "E228", {"start": v(4.5, 0) * mm, "end": v(4.5, 6) * mm});
            skLineSegment(sketch, "E229", {"start": v(4.5, 6) * mm, "end": v(1, 6) * mm});
            skLineSegment(sketch, "E230", {"start": v(1, 6) * mm, "end": v(1, 24.49) * mm});
            skPoint(sketch, "E231.visualSharp", {"position": v(1, 28.85) * mm});
            skArc(sketch, "E231.filletArc", {"start": v(1, 24.49) * mm, "mid": v(-0.05, 27.55) * mm, "end": v(-2.75, 29.33) * mm});
            skPoint(sketch, "E232", {"position": v(16.5, 16) * mm});
            skLineSegment(sketch, "E233", {"start": v(16.5, 16) * mm, "end": v(16.5, 0) * mm, "construction": true});
            skSolve(sketch);
        }
        {
            var Q0;
            Q0 = qSketchRegion(id + "F11", true);
            var Q1;
            Q1=makeQuery(id+"F1.opExtrude","SWEPT_FACE",FACE,{"disambiguationData":[OSD([sQuery(id+"F0.wireOp",EDGE,"E60.left")])]});
            extrude(context, id + "F12", {"entities" : qUnion([Q0]), "endBound" : BoundingType.UP_TO_SURFACE, "endBoundEntityFace" : qUnion([Q1]), "depth" : 25 * mm});
        }
        {
            var Q0;
            Q0=makeQuery(id+"F12.opExtrude","SWEPT_BODY",BODY,{"disambiguationData":[OSD([sQuery(id+"F11.wireOp",EDGE,"E194"),sQuery(id+"F11.wireOp",EDGE,"E195"),sQuery(id+"F11.wireOp",EDGE,"E196"),sQuery(id+"F11.wireOp",EDGE,"E197"),sQuery(id+"F11.wireOp",EDGE,"E198"),sQuery(id+"F11.wireOp",EDGE,"E199"),sQuery(id+"F11.wireOp",EDGE,"E200"),sQuery(id+"F11.wireOp",EDGE,"E201"),sQuery(id+"F11.wireOp",EDGE,"E202"),sQuery(id+"F11.wireOp",EDGE,"E203.filletArc"),sQuery(id+"F11.wireOp",EDGE,"E204"),sQuery(id+"F11.wireOp",EDGE,"E205"),sQuery(id+"F11.wireOp",EDGE,"E208"),sQuery(id+"F11.wireOp",EDGE,"E209"),sQuery(id+"F11.wireOp",EDGE,"E210"),sQuery(id+"F11.wireOp",EDGE,"E211"),sQuery(id+"F11.wireOp",EDGE,"E212"),sQuery(id+"F11.wireOp",EDGE,"E213"),sQuery(id+"F11.wireOp",EDGE,"E214"),sQuery(id+"F11.wireOp",EDGE,"E215"),sQuery(id+"F11.wireOp",EDGE,"E216"),sQuery(id+"F11.wireOp",EDGE,"E217"),sQuery(id+"F11.wireOp",EDGE,"E218"),sQuery(id+"F11.wireOp",EDGE,"E219"),sQuery(id+"F11.wireOp",EDGE,"E220"),sQuery(id+"F11.wireOp",EDGE,"E221"),sQuery(id+"F11.wireOp",EDGE,"E222"),sQuery(id+"F11.wireOp",EDGE,"E223"),sQuery(id+"F11.wireOp",EDGE,"E224"),sQuery(id+"F11.wireOp",EDGE,"E225"),sQuery(id+"F11.wireOp",EDGE,"E226"),sQuery(id+"F11.wireOp",EDGE,"E227"),sQuery(id+"F11.wireOp",EDGE,"E228"),sQuery(id+"F11.wireOp",EDGE,"E229"),sQuery(id+"F11.wireOp",EDGE,"E230"),sQuery(id+"F11.wireOp",EDGE,"E231.filletArc")])]});
            var Q1;
            Q1=makeQuery(id+"F6.opExtrude","SWEPT_BODY",BODY,{"disambiguationData":[OSD([sQuery(id+"F5.wireOp",EDGE,"E141"),sQuery(id+"F5.wireOp",EDGE,"E142"),sQuery(id+"F5.wireOp",EDGE,"E143"),sQuery(id+"F5.wireOp",EDGE,"E144"),sQuery(id+"F5.wireOp",EDGE,"E146"),sQuery(id+"F5.wireOp",EDGE,"E147"),sQuery(id+"F5.wireOp",EDGE,"E148"),sQuery(id+"F5.wireOp",EDGE,"E149"),sQuery(id+"F5.wireOp",EDGE,"E150"),sQuery(id+"F5.wireOp",EDGE,"E151"),sQuery(id+"F5.wireOp",EDGE,"E152"),sQuery(id+"F5.wireOp",EDGE,"E153"),sQuery(id+"F5.wireOp",EDGE,"E154"),sQuery(id+"F5.wireOp",EDGE,"E155"),sQuery(id+"F5.wireOp",EDGE,"E156"),sQuery(id+"F5.wireOp",EDGE,"E157"),sQuery(id+"F5.wireOp",EDGE,"E158"),sQuery(id+"F5.wireOp",EDGE,"E159"),sQuery(id+"F5.wireOp",EDGE,"E160"),sQuery(id+"F5.wireOp",EDGE,"E161"),sQuery(id+"F5.wireOp",EDGE,"E162"),sQuery(id+"F5.wireOp",EDGE,"E164.MirrorCS"),sQuery(id+"F5.wireOp",EDGE,"E165.MirrorCS"),sQuery(id+"F5.wireOp",EDGE,"E166.MirrorCS"),sQuery(id+"F5.wireOp",EDGE,"E167.MirrorCS"),sQuery(id+"F5.wireOp",EDGE,"E168.MirrorCS"),sQuery(id+"F5.wireOp",EDGE,"E169.MirrorCS"),sQuery(id+"F5.wireOp",EDGE,"E170.MirrorCS"),sQuery(id+"F5.wireOp",EDGE,"E171.MirrorCS"),sQuery(id+"F5.wireOp",EDGE,"E172.MirrorCS"),sQuery(id+"F5.wireOp",EDGE,"E173.MirrorCS"),sQuery(id+"F5.wireOp",EDGE,"E174.MirrorCS"),sQuery(id+"F5.wireOp",EDGE,"E175.MirrorCS"),sQuery(id+"F5.wireOp",EDGE,"E176.MirrorCS"),sQuery(id+"F5.wireOp",EDGE,"E177.MirrorCS"),sQuery(id+"F5.wireOp",EDGE,"E178.MirrorCS"),sQuery(id+"F5.wireOp",EDGE,"E179.MirrorCS"),sQuery(id+"F5.wireOp",EDGE,"E180.MirrorCS"),sQuery(id+"F5.wireOp",EDGE,"E181.MirrorCS"),sQuery(id+"F5.wireOp",EDGE,"E182.MirrorCS"),sQuery(id+"F5.wireOp",EDGE,"E183.filletArc"),sQuery(id+"F5.wireOp",EDGE,"E184.filletArc"),sQuery(id+"F5.wireOp",EDGE,"E185"),sQuery(id+"F5.wireOp",EDGE,"E186")])]});
            booleanBodies(context, id + "F13", {"operationType" : BooleanOperationType.SUBTRACTION, "tools" : qUnion([Q0]), "targets" : qUnion([Q1]), "keepTools" : true});
        }
        {
            var Q0;
            Q0=makeQuery(id+"F11.imprint","IMPRINT",FACE,{"disambiguationData":[TD([[makeQuery(id+"F11.imprint","IMPRINT",EDGE,{"derivedFrom":sQuery(id+"F11.wireOp",EDGE,"E210")}),1.0]])]});
            var Q1;
            Q1=makeQuery(id+"F11.imprint","IMPRINT",FACE,{"disambiguationData":[TD([[makeQuery(id+"F11.imprint","IMPRINT",EDGE,{"derivedFrom":sQuery(id+"F11.wireOp",EDGE,"E208")}),1.0]])]});
            var Q2;
            Q2=makeQuery(id+"F11.imprint","IMPRINT",FACE,{"disambiguationData":[TD([[makeQuery(id+"F11.imprint","IMPRINT",EDGE,{"derivedFrom":sQuery(id+"F11.wireOp",EDGE,"E209")}),1.0]])]});
            var Q3;
            Q3=makeQuery(id+"F11.imprint","IMPRINT",FACE,{"disambiguationData":[TD([[makeQuery(id+"F11.imprint","IMPRINT",EDGE,{"derivedFrom":sQuery(id+"F11.wireOp",EDGE,"E204")}),1.0]])]});
            var Q4;
            Q4=makeQuery(id+"F3.opExtrude","CAP_FACE",FACE,{"disambiguationData":[OSD([sQuery(id+"F2.wireOp",EDGE,"E84"),sQuery(id+"F2.wireOp",EDGE,"E85"),sQuery(id+"F2.wireOp",EDGE,"E86"),sQuery(id+"F2.wireOp",EDGE,"E87"),sQuery(id+"F2.wireOp",EDGE,"E88"),sQuery(id+"F2.wireOp",EDGE,"E89"),sQuery(id+"F2.wireOp",EDGE,"E90"),sQuery(id+"F2.wireOp",EDGE,"E91"),sQuery(id+"F2.wireOp",EDGE,"E92"),sQuery(id+"F2.wireOp",EDGE,"E93"),sQuery(id+"F2.wireOp",EDGE,"E94"),sQuery(id+"F2.wireOp",EDGE,"E95"),sQuery(id+"F2.wireOp",EDGE,"E96"),sQuery(id+"F2.wireOp",EDGE,"E97"),sQuery(id+"F2.wireOp",EDGE,"E98"),sQuery(id+"F2.wireOp",EDGE,"E100.MirrorCS"),sQuery(id+"F2.wireOp",EDGE,"E101.MirrorCS"),sQuery(id+"F2.wireOp",EDGE,"E102.MirrorCS"),sQuery(id+"F2.wireOp",EDGE,"E103.MirrorCS"),sQuery(id+"F2.wireOp",EDGE,"E104.MirrorCS"),sQuery(id+"F2.wireOp",EDGE,"E105.MirrorCS"),sQuery(id+"F2.wireOp",EDGE,"E106.MirrorCS"),sQuery(id+"F2.wireOp",EDGE,"E107.MirrorCS"),sQuery(id+"F2.wireOp",EDGE,"E108.MirrorCS"),sQuery(id+"F2.wireOp",EDGE,"E109.MirrorCS"),sQuery(id+"F2.wireOp",EDGE,"E110.MirrorCS"),sQuery(id+"F2.wireOp",EDGE,"E111.MirrorCS"),sQuery(id+"F2.wireOp",EDGE,"E112.MirrorCS"),sQuery(id+"F2.wireOp",EDGE,"E113"),sQuery(id+"F2.wireOp",EDGE,"E114"),sQuery(id+"F2.wireOp",EDGE,"E115"),sQuery(id+"F2.wireOp",EDGE,"E116"),sQuery(id+"F2.wireOp",EDGE,"E117"),sQuery(id+"F2.wireOp",EDGE,"E121.MirrorCS"),sQuery(id+"F2.wireOp",EDGE,"E122.MirrorCS"),sQuery(id+"F2.wireOp",EDGE,"E123.MirrorCS"),sQuery(id+"F2.wireOp",EDGE,"E124.MirrorCS"),sQuery(id+"F2.wireOp",EDGE,"E126.MirrorCS"),sQuery(id+"F2.wireOp",EDGE,"E128.MirrorCS"),sQuery(id+"F2.wireOp",EDGE,"E129.MirrorCS"),sQuery(id+"F2.wireOp",EDGE,"E132.MirrorCS"),sQuery(id+"F2.wireOp",EDGE,"E133.MirrorCS"),sQuery(id+"F2.wireOp",EDGE,"E134.MirrorC"),sQuery(id+"F2.wireOp",EDGE,"E135.MirrorCS"),sQuery(id+"F2.wireOp",EDGE,"E137.MirrorCS"),sQuery(id+"F2.wireOp",EDGE,"E138.MirrorCS"),sQuery(id+"F2.wireOp",EDGE,"E139"),sQuery(id+"F2.wireOp",EDGE,"E140")])],"isStart":false});
            extrude(context, id + "F14", {"entities" : qUnion([Q0, Q1, Q2, Q3]), "operationType" : NewBodyOperationType.REMOVE, "endBound" : BoundingType.UP_TO_SURFACE, "endBoundEntityFace" : qUnion([Q4]), "depth" : 25 * mm});
        }
    });
